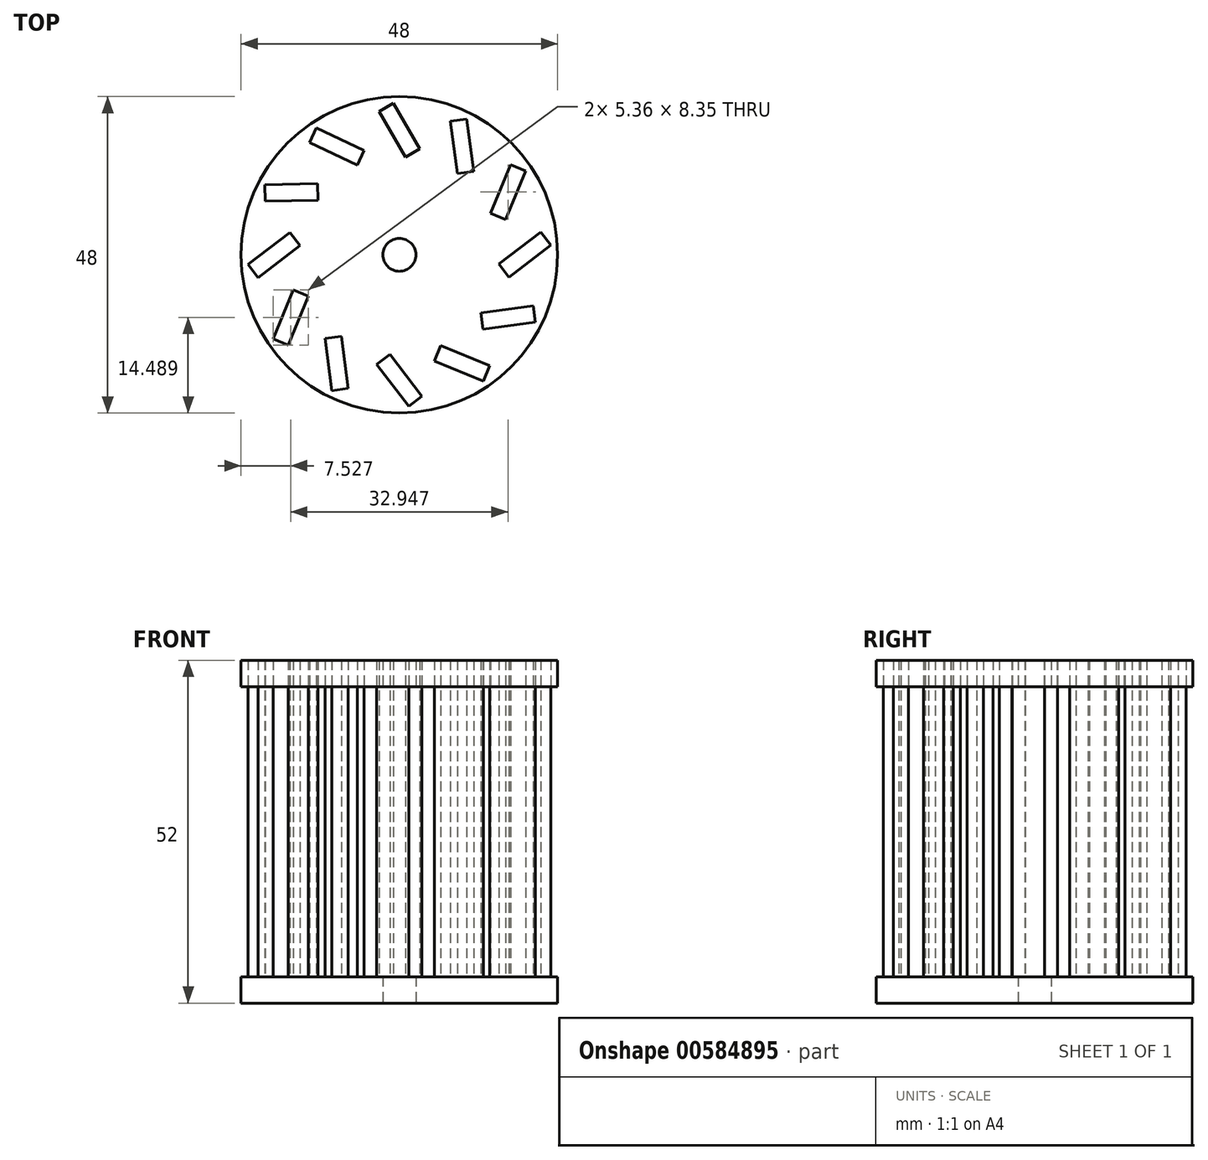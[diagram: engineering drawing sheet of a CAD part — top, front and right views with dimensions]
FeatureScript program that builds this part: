
annotation { "Feature Type Name" : "Feature", "Feature Type Description" : "" }
export const myFeature = defineFeature(function(context is Context, id is Id, definition is map)
    precondition{}
    {
        {
            var Q0;
            Q0=qCreatedBy(makeId("Top.planeOp"),FACE);
            var sketch = newSketch(context, id + "F0", { "sketchPlane" : qUnion([Q0])});
            skCircle(sketch, "E0", {"center": v(0, 0) * mm, "radius": 24 * mm});
            skArc(sketch, "E1", {"start": v(22.95, 1.48) * mm, "mid": v(-22.55, 4.53) * mm, "end": v(20.6, -10.23) * mm});
            skLineSegment(sketch, "E2", {"start": v(-3.08, 21.73) * mm, "end": v(-3.08, 14.8) * mm});
            skLineSegment(sketch, "E3", {"start": v(-3.08, 14.8) * mm, "end": v(0.92, 14.8) * mm});
            skLineSegment(sketch, "E4", {"start": v(0.92, 14.8) * mm, "end": v(-3.08, 21.73) * mm});
            skLineSegment(sketch, "E5", {"start": v(0.92, 14.8) * mm, "end": v(3.08, 16.05) * mm});
            skLineSegment(sketch, "E6", {"start": v(3.08, 16.05) * mm, "end": v(-0.92, 22.98) * mm});
            skLineSegment(sketch, "E7", {"start": v(-0.92, 22.98) * mm, "end": v(-3.08, 21.73) * mm});
            skLineSegment(sketch, "E8", {"start": v(-2, 22.36) * mm, "end": v(2, 15.43) * mm});
            skLineSegment(sketch, "E9", {"start": v(1.08, 19.52) * mm, "end": v(-1.08, 18.27) * mm});
            skPoint(sketch, "E10", {"position": v(0, 18.9) * mm});
            skLineSegment(sketch, "E11", {"start": v(1.04, 0.6) * mm, "end": v(-1.02, -0.59) * mm});
            skLineSegment(sketch, "E12.MirrorCS", {"start": v(-16.61, 3.4) * mm, "end": v(-22.95, -1.47) * mm});
            skLineSegment(sketch, "E13.MirrorCS", {"start": v(-15.09, 1.43) * mm, "end": v(-21.43, -3.46) * mm});
            skLineSegment(sketch, "E14.MirrorCS", {"start": v(-15.09, 1.43) * mm, "end": v(-16.61, 3.4) * mm});
            skLineSegment(sketch, "E15.MirrorCS", {"start": v(-22.95, -1.47) * mm, "end": v(-21.43, -3.46) * mm});
            skLineSegment(sketch, "E16.MirrorCS", {"start": v(-15.85, 2.42) * mm, "end": v(-22.2, -2.46) * mm});
            skLineSegment(sketch, "E17.MirrorCS", {"start": v(-18.23, -1) * mm, "end": v(-19.75, 1) * mm});
            skPoint(sketch, "E18.MirrorP", {"position": v(-18.99, 0) * mm});
            skLineSegment(sketch, "E19.MirrorCS", {"start": v(16.61, -3.4) * mm, "end": v(22.95, 1.48) * mm});
            skLineSegment(sketch, "E20.MirrorCS", {"start": v(15.1, -1.41) * mm, "end": v(21.43, 3.47) * mm});
            skLineSegment(sketch, "E21.MirrorCS", {"start": v(15.1, -1.41) * mm, "end": v(16.61, -3.4) * mm});
            skLineSegment(sketch, "E22.MirrorCS", {"start": v(22.95, 1.48) * mm, "end": v(21.43, 3.47) * mm});
            skLineSegment(sketch, "E23.MirrorCS", {"start": v(15.85, -2.4) * mm, "end": v(22.2, 2.48) * mm});
            skLineSegment(sketch, "E24.MirrorCS", {"start": v(18.22, 1) * mm, "end": v(19.74, -1) * mm});
            skPoint(sketch, "E25", {"position": v(18.98, 0) * mm});
            skLineSegment(sketch, "E26.MirrorCS", {"start": v(16.1, 5.34) * mm, "end": v(19.15, 12.73) * mm});
            skLineSegment(sketch, "E27.MirrorCS", {"start": v(13.8, 6.29) * mm, "end": v(16.84, 13.69) * mm});
            skLineSegment(sketch, "E28.MirrorCS", {"start": v(13.8, 6.29) * mm, "end": v(16.1, 5.34) * mm});
            skLineSegment(sketch, "E29.MirrorCS", {"start": v(19.15, 12.73) * mm, "end": v(16.84, 13.69) * mm});
            skLineSegment(sketch, "E30.MirrorCS", {"start": v(14.95, 5.81) * mm, "end": v(18, 13.2) * mm});
            skLineSegment(sketch, "E31.MirrorCS", {"start": v(15.32, 9.99) * mm, "end": v(17.63, 9.03) * mm});
            skPoint(sketch, "E32", {"position": v(16.47, 9.51) * mm});
            skLineSegment(sketch, "E33.MirrorCS", {"start": v(11.28, 12.67) * mm, "end": v(10.22, 20.6) * mm});
            skLineSegment(sketch, "E34.MirrorCS", {"start": v(8.8, 12.34) * mm, "end": v(7.74, 20.27) * mm});
            skLineSegment(sketch, "E35.MirrorCS", {"start": v(8.8, 12.34) * mm, "end": v(11.28, 12.67) * mm});
            skLineSegment(sketch, "E36.MirrorCS", {"start": v(10.22, 20.6) * mm, "end": v(7.74, 20.27) * mm});
            skLineSegment(sketch, "E37.MirrorCS", {"start": v(10.04, 12.5) * mm, "end": v(8.98, 20.44) * mm});
            skLineSegment(sketch, "E38.MirrorCS", {"start": v(8.27, 16.3) * mm, "end": v(10.75, 16.64) * mm});
            skPoint(sketch, "E39", {"position": v(9.51, 16.47) * mm});
            skLineSegment(sketch, "E40", {"start": v(-0.67, -1.16) * mm, "end": v(0.63, 1.1) * mm});
            skLineSegment(sketch, "E41", {"start": v(1.07, -0.62) * mm, "end": v(-1.13, 0.65) * mm});
            skLineSegment(sketch, "E42", {"start": v(0.67, -1.16) * mm, "end": v(-0.59, 1.02) * mm});
            skLineSegment(sketch, "E43.MirrorCS", {"start": v(12.67, -11.27) * mm, "end": v(20.6, -10.23) * mm});
            skLineSegment(sketch, "E44.MirrorCS", {"start": v(12.34, -8.8) * mm, "end": v(20.27, -7.75) * mm});
            skLineSegment(sketch, "E45.MirrorCS", {"start": v(12.34, -8.8) * mm, "end": v(12.67, -11.27) * mm});
            skLineSegment(sketch, "E46.MirrorCS", {"start": v(20.6, -10.23) * mm, "end": v(20.27, -7.75) * mm});
            skLineSegment(sketch, "E47.MirrorCS", {"start": v(12.5, -10.03) * mm, "end": v(20.44, -8.99) * mm});
            skLineSegment(sketch, "E48.MirrorCS", {"start": v(16.3, -8.27) * mm, "end": v(16.64, -10.75) * mm});
            skPoint(sketch, "E49", {"position": v(16.47, -9.51) * mm});
            skLineSegment(sketch, "E50.MirrorCS", {"start": v(5.34, -16.1) * mm, "end": v(12.73, -19.15) * mm});
            skLineSegment(sketch, "E51.MirrorCS", {"start": v(6.3, -13.8) * mm, "end": v(13.69, -16.84) * mm});
            skLineSegment(sketch, "E52.MirrorCS", {"start": v(6.3, -13.8) * mm, "end": v(5.34, -16.1) * mm});
            skLineSegment(sketch, "E53.MirrorCS", {"start": v(12.73, -19.15) * mm, "end": v(13.69, -16.84) * mm});
            skLineSegment(sketch, "E54.MirrorCS", {"start": v(5.81, -14.95) * mm, "end": v(13.2, -18) * mm});
            skLineSegment(sketch, "E55.MirrorCS", {"start": v(9.99, -15.32) * mm, "end": v(9.03, -17.63) * mm});
            skPoint(sketch, "E56", {"position": v(9.51, -16.47) * mm});
            skLineSegment(sketch, "E57.MirrorCS", {"start": v(-16.84, -13.69) * mm, "end": v(-13.8, -6.3) * mm});
            skLineSegment(sketch, "E58.MirrorCS", {"start": v(-19.15, -12.73) * mm, "end": v(-16.1, -5.34) * mm});
            skLineSegment(sketch, "E59.MirrorCS", {"start": v(-19.15, -12.73) * mm, "end": v(-16.84, -13.69) * mm});
            skLineSegment(sketch, "E60.MirrorCS", {"start": v(-13.8, -6.3) * mm, "end": v(-16.1, -5.34) * mm});
            skLineSegment(sketch, "E61.MirrorCS", {"start": v(-18, -13.2) * mm, "end": v(-14.95, -5.81) * mm});
            skLineSegment(sketch, "E62.MirrorCS", {"start": v(-17.63, -9.03) * mm, "end": v(-15.32, -9.99) * mm});
            skPoint(sketch, "E63", {"position": v(-16.47, -9.51) * mm});
            skLineSegment(sketch, "E64.MirrorCS", {"start": v(-7.74, -20.27) * mm, "end": v(-8.8, -12.34) * mm});
            skLineSegment(sketch, "E65.MirrorCS", {"start": v(-10.22, -20.6) * mm, "end": v(-11.28, -12.67) * mm});
            skLineSegment(sketch, "E66.MirrorCS", {"start": v(-10.22, -20.6) * mm, "end": v(-7.74, -20.27) * mm});
            skLineSegment(sketch, "E67.MirrorCS", {"start": v(-8.8, -12.34) * mm, "end": v(-11.28, -12.67) * mm});
            skLineSegment(sketch, "E68.MirrorCS", {"start": v(-8.98, -20.44) * mm, "end": v(-10.04, -12.5) * mm});
            skLineSegment(sketch, "E69.MirrorCS", {"start": v(-10.75, -16.64) * mm, "end": v(-8.27, -16.3) * mm});
            skPoint(sketch, "E70", {"position": v(-9.51, -16.47) * mm});
            skLineSegment(sketch, "E71.MirrorCS", {"start": v(-20.35, 8.11) * mm, "end": v(-12.35, 8.3) * mm});
            skLineSegment(sketch, "E72.MirrorCS", {"start": v(-20.4, 10.61) * mm, "end": v(-12.4, 10.8) * mm});
            skLineSegment(sketch, "E73.MirrorCS", {"start": v(-20.4, 10.61) * mm, "end": v(-20.35, 8.11) * mm});
            skLineSegment(sketch, "E74.MirrorCS", {"start": v(-12.35, 8.3) * mm, "end": v(-12.4, 10.8) * mm});
            skLineSegment(sketch, "E75.MirrorCS", {"start": v(-20.38, 9.36) * mm, "end": v(-12.38, 9.55) * mm});
            skLineSegment(sketch, "E76.MirrorCS", {"start": v(-16.4, 10.7) * mm, "end": v(-16.35, 8.2) * mm});
            skPoint(sketch, "E77", {"position": v(-16.38, 9.46) * mm});
            skLineSegment(sketch, "E78.MirrorCS", {"start": v(-13.63, 17) * mm, "end": v(-6.4, 13.59) * mm});
            skLineSegment(sketch, "E79.MirrorCS", {"start": v(-12.57, 19.26) * mm, "end": v(-5.33, 15.85) * mm});
            skLineSegment(sketch, "E80.MirrorCS", {"start": v(-12.57, 19.26) * mm, "end": v(-13.63, 17) * mm});
            skLineSegment(sketch, "E81.MirrorCS", {"start": v(-6.4, 13.59) * mm, "end": v(-5.33, 15.85) * mm});
            skLineSegment(sketch, "E82.MirrorCS", {"start": v(-13.1, 18.13) * mm, "end": v(-5.87, 14.72) * mm});
            skLineSegment(sketch, "E83.MirrorCS", {"start": v(-8.95, 17.56) * mm, "end": v(-10.02, 15.3) * mm});
            skPoint(sketch, "E84", {"position": v(-9.48, 16.43) * mm});
            skCircle(sketch, "E85", {"center": v(0, 0) * mm, "radius": 2.5 * mm});
            skLineSegment(sketch, "E86.MirrorCS", {"start": v(3.43, -21.43) * mm, "end": v(-1.45, -15.1) * mm});
            skLineSegment(sketch, "E87.MirrorCS", {"start": v(1.45, -22.95) * mm, "end": v(-3.43, -16.62) * mm});
            skLineSegment(sketch, "E88.MirrorCS", {"start": v(1.45, -22.95) * mm, "end": v(3.43, -21.43) * mm});
            skLineSegment(sketch, "E89.MirrorCS", {"start": v(-1.45, -15.1) * mm, "end": v(-3.43, -16.62) * mm});
            skLineSegment(sketch, "E90.MirrorCS", {"start": v(2.44, -22.2) * mm, "end": v(-2.44, -15.85) * mm});
            skLineSegment(sketch, "E91.MirrorCS", {"start": v(-1, -19.79) * mm, "end": v(1, -18.26) * mm});
            skPoint(sketch, "E92", {"position": v(0, -19.02) * mm});
            skSolve(sketch);
        }
        {
            var Q0;
            Q0=makeQuery(id+"F0.imprint","IMPRINT",FACE,{"disambiguationData":[TD([[makeQuery(id+"F0.imprint","IMPRINT",EDGE,{"derivedFrom":sQuery(id+"F0.wireOp",EDGE,"E0")}),1.0]])]});
            var Q1;
            {var subQ0=sQuery(id+"F0.wireOp",EDGE,"E2");Q1=makeQuery(id+"F0.imprint","IMPRINT",FACE,{"disambiguationData":[TD([[makeQuery(id+"F0.imprint","IMPRINT",EDGE,{"derivedFrom":subQ0}),1.0]])]});}
            extrude(context, id + "F1", {"entities" : qUnion([Q0, Q1]), "depth" : 4 * mm, "offsetDistance" : 25 * mm});
        }
        {
            var Q0;
            {var subQ0=sQuery(id+"F0.wireOp",EDGE,"E35.MirrorCS");var subQ1=sQuery(id+"F0.wireOp",EDGE,"E33.MirrorCS");var subQ2=makeQuery(id+"F0.imprint","INTERSECT",VERTEX,{"derivedFrom":[subQ1,subQ0]});Q0=makeQuery(id+"F0.imprint","IMPRINT",FACE,{"disambiguationData":[TD([[makeQuery(id+"F0.imprint","IMPRINT",EDGE,{"disambiguationData":[TD([[subQ2,-1.0]])],"derivedFrom":subQ1}),1.0]])]});}
            var Q1;
            {var subQ0=sQuery(id+"F0.wireOp",EDGE,"E35.MirrorCS");var subQ1=sQuery(id+"F0.wireOp",EDGE,"E34.MirrorCS");var subQ2=makeQuery(id+"F0.imprint","INTERSECT",VERTEX,{"derivedFrom":[subQ1,subQ0]});Q1=makeQuery(id+"F0.imprint","IMPRINT",FACE,{"disambiguationData":[TD([[makeQuery(id+"F0.imprint","IMPRINT",EDGE,{"disambiguationData":[TD([[subQ2,-1.0]])],"derivedFrom":subQ1}),-1.0]])]});}
            var Q2;
            {var subQ0=sQuery(id+"F0.wireOp",EDGE,"E36.MirrorCS");var subQ1=sQuery(id+"F0.wireOp",EDGE,"E33.MirrorCS");var subQ2=makeQuery(id+"F0.imprint","INTERSECT",VERTEX,{"derivedFrom":[subQ1,subQ0]});Q2=makeQuery(id+"F0.imprint","IMPRINT",FACE,{"disambiguationData":[TD([[makeQuery(id+"F0.imprint","IMPRINT",EDGE,{"disambiguationData":[TD([[subQ2,1.0]])],"derivedFrom":subQ1}),1.0]])]});}
            var Q3;
            {var subQ0=sQuery(id+"F0.wireOp",EDGE,"E36.MirrorCS");var subQ1=sQuery(id+"F0.wireOp",EDGE,"E34.MirrorCS");var subQ2=makeQuery(id+"F0.imprint","INTERSECT",VERTEX,{"derivedFrom":[subQ1,subQ0]});Q3=makeQuery(id+"F0.imprint","IMPRINT",FACE,{"disambiguationData":[TD([[makeQuery(id+"F0.imprint","IMPRINT",EDGE,{"disambiguationData":[TD([[subQ2,1.0]])],"derivedFrom":subQ1}),-1.0]])]});}
            var Q4;
            {var subQ0=sQuery(id+"F0.wireOp",EDGE,"E6");var subQ1=sQuery(id+"F0.wireOp",EDGE,"E5");var subQ2=makeQuery(id+"F0.imprint","INTERSECT",VERTEX,{"derivedFrom":[subQ1,subQ0]});Q4=makeQuery(id+"F0.imprint","IMPRINT",FACE,{"disambiguationData":[TD([[makeQuery(id+"F0.imprint","IMPRINT",EDGE,{"disambiguationData":[TD([[subQ2,1.0]])],"derivedFrom":subQ1}),1.0]])]});}
            var Q5;
            {var subQ0=sQuery(id+"F0.wireOp",EDGE,"E5");var subQ5=sQuery(id+"F0.wireOp",EDGE,"E8");var subQ6=makeQuery(id+"F0.imprint","INTERSECT",VERTEX,{"derivedFrom":[subQ0,subQ5]});Q5=makeQuery(id+"F0.imprint","IMPRINT",FACE,{"disambiguationData":[TD([[makeQuery(id+"F0.imprint","IMPRINT",EDGE,{"disambiguationData":[TD([[subQ6,1.0]])],"derivedFrom":subQ5}),-1.0]])]});}
            var Q6;
            {var subQ0=sQuery(id+"F0.wireOp",EDGE,"E7");var subQ1=sQuery(id+"F0.wireOp",EDGE,"E6");var subQ2=makeQuery(id+"F0.imprint","INTERSECT",VERTEX,{"derivedFrom":[subQ1,subQ0]});Q6=makeQuery(id+"F0.imprint","IMPRINT",FACE,{"disambiguationData":[TD([[makeQuery(id+"F0.imprint","IMPRINT",EDGE,{"disambiguationData":[TD([[subQ2,1.0]])],"derivedFrom":subQ1}),1.0]])]});}
            var Q7;
            {var subQ0=sQuery(id+"F0.wireOp",EDGE,"E7");var subQ5=sQuery(id+"F0.wireOp",EDGE,"E8");var subQ7=makeQuery(id+"F0.imprint","INTERSECT",VERTEX,{"derivedFrom":[subQ0,subQ5]});Q7=makeQuery(id+"F0.imprint","IMPRINT",FACE,{"disambiguationData":[TD([[makeQuery(id+"F0.imprint","IMPRINT",EDGE,{"disambiguationData":[TD([[subQ7,-1.0]])],"derivedFrom":subQ5}),-1.0]])]});}
            var Q8;
            {var subQ0=sQuery(id+"F0.wireOp",EDGE,"E80.MirrorCS");var subQ1=sQuery(id+"F0.wireOp",EDGE,"E79.MirrorCS");var subQ2=makeQuery(id+"F0.imprint","INTERSECT",VERTEX,{"derivedFrom":[subQ1,subQ0]});Q8=makeQuery(id+"F0.imprint","IMPRINT",FACE,{"disambiguationData":[TD([[makeQuery(id+"F0.imprint","IMPRINT",EDGE,{"disambiguationData":[TD([[subQ2,-1.0]])],"derivedFrom":subQ1}),-1.0]])]});}
            var Q9;
            {var subQ0=sQuery(id+"F0.wireOp",EDGE,"E80.MirrorCS");var subQ1=sQuery(id+"F0.wireOp",EDGE,"E78.MirrorCS");var subQ2=makeQuery(id+"F0.imprint","INTERSECT",VERTEX,{"derivedFrom":[subQ1,subQ0]});Q9=makeQuery(id+"F0.imprint","IMPRINT",FACE,{"disambiguationData":[TD([[makeQuery(id+"F0.imprint","IMPRINT",EDGE,{"disambiguationData":[TD([[subQ2,-1.0]])],"derivedFrom":subQ1}),1.0]])]});}
            var Q10;
            {var subQ0=sQuery(id+"F0.wireOp",EDGE,"E81.MirrorCS");var subQ1=sQuery(id+"F0.wireOp",EDGE,"E79.MirrorCS");var subQ2=makeQuery(id+"F0.imprint","INTERSECT",VERTEX,{"derivedFrom":[subQ1,subQ0]});Q10=makeQuery(id+"F0.imprint","IMPRINT",FACE,{"disambiguationData":[TD([[makeQuery(id+"F0.imprint","IMPRINT",EDGE,{"disambiguationData":[TD([[subQ2,1.0]])],"derivedFrom":subQ1}),-1.0]])]});}
            var Q11;
            {var subQ0=sQuery(id+"F0.wireOp",EDGE,"E81.MirrorCS");var subQ1=sQuery(id+"F0.wireOp",EDGE,"E78.MirrorCS");var subQ2=makeQuery(id+"F0.imprint","INTERSECT",VERTEX,{"derivedFrom":[subQ1,subQ0]});Q11=makeQuery(id+"F0.imprint","IMPRINT",FACE,{"disambiguationData":[TD([[makeQuery(id+"F0.imprint","IMPRINT",EDGE,{"disambiguationData":[TD([[subQ2,1.0]])],"derivedFrom":subQ1}),1.0]])]});}
            var Q12;
            {var subQ0=sQuery(id+"F0.wireOp",EDGE,"E74.MirrorCS");var subQ1=sQuery(id+"F0.wireOp",EDGE,"E72.MirrorCS");var subQ2=makeQuery(id+"F0.imprint","INTERSECT",VERTEX,{"derivedFrom":[subQ1,subQ0]});Q12=makeQuery(id+"F0.imprint","IMPRINT",FACE,{"disambiguationData":[TD([[makeQuery(id+"F0.imprint","IMPRINT",EDGE,{"disambiguationData":[TD([[subQ2,1.0]])],"derivedFrom":subQ1}),-1.0]])]});}
            var Q13;
            {var subQ0=sQuery(id+"F0.wireOp",EDGE,"E73.MirrorCS");var subQ1=sQuery(id+"F0.wireOp",EDGE,"E72.MirrorCS");var subQ2=makeQuery(id+"F0.imprint","INTERSECT",VERTEX,{"derivedFrom":[subQ1,subQ0]});Q13=makeQuery(id+"F0.imprint","IMPRINT",FACE,{"disambiguationData":[TD([[makeQuery(id+"F0.imprint","IMPRINT",EDGE,{"disambiguationData":[TD([[subQ2,-1.0]])],"derivedFrom":subQ1}),-1.0]])]});}
            var Q14;
            {var subQ0=sQuery(id+"F0.wireOp",EDGE,"E73.MirrorCS");var subQ1=sQuery(id+"F0.wireOp",EDGE,"E71.MirrorCS");var subQ2=makeQuery(id+"F0.imprint","INTERSECT",VERTEX,{"derivedFrom":[subQ1,subQ0]});Q14=makeQuery(id+"F0.imprint","IMPRINT",FACE,{"disambiguationData":[TD([[makeQuery(id+"F0.imprint","IMPRINT",EDGE,{"disambiguationData":[TD([[subQ2,-1.0]])],"derivedFrom":subQ1}),1.0]])]});}
            var Q15;
            {var subQ0=sQuery(id+"F0.wireOp",EDGE,"E74.MirrorCS");var subQ1=sQuery(id+"F0.wireOp",EDGE,"E71.MirrorCS");var subQ2=makeQuery(id+"F0.imprint","INTERSECT",VERTEX,{"derivedFrom":[subQ1,subQ0]});Q15=makeQuery(id+"F0.imprint","IMPRINT",FACE,{"disambiguationData":[TD([[makeQuery(id+"F0.imprint","IMPRINT",EDGE,{"disambiguationData":[TD([[subQ2,1.0]])],"derivedFrom":subQ1}),1.0]])]});}
            var Q16;
            {var subQ0=sQuery(id+"F0.wireOp",EDGE,"E14.MirrorCS");var subQ1=sQuery(id+"F0.wireOp",EDGE,"E12.MirrorCS");var subQ2=makeQuery(id+"F0.imprint","INTERSECT",VERTEX,{"derivedFrom":[subQ1,subQ0]});Q16=makeQuery(id+"F0.imprint","IMPRINT",FACE,{"disambiguationData":[TD([[makeQuery(id+"F0.imprint","IMPRINT",EDGE,{"disambiguationData":[TD([[subQ2,-1.0]])],"derivedFrom":subQ1}),1.0]])]});}
            var Q17;
            {var subQ0=sQuery(id+"F0.wireOp",EDGE,"E15.MirrorCS");var subQ1=sQuery(id+"F0.wireOp",EDGE,"E12.MirrorCS");var subQ2=makeQuery(id+"F0.imprint","INTERSECT",VERTEX,{"derivedFrom":[subQ1,subQ0]});Q17=makeQuery(id+"F0.imprint","IMPRINT",FACE,{"disambiguationData":[TD([[makeQuery(id+"F0.imprint","IMPRINT",EDGE,{"disambiguationData":[TD([[subQ2,1.0]])],"derivedFrom":subQ1}),1.0]])]});}
            var Q18;
            {var subQ0=sQuery(id+"F0.wireOp",EDGE,"E15.MirrorCS");var subQ1=sQuery(id+"F0.wireOp",EDGE,"E13.MirrorCS");var subQ2=makeQuery(id+"F0.imprint","INTERSECT",VERTEX,{"derivedFrom":[subQ1,subQ0]});Q18=makeQuery(id+"F0.imprint","IMPRINT",FACE,{"disambiguationData":[TD([[makeQuery(id+"F0.imprint","IMPRINT",EDGE,{"disambiguationData":[TD([[subQ2,1.0]])],"derivedFrom":subQ1}),-1.0]])]});}
            var Q19;
            {var subQ0=sQuery(id+"F0.wireOp",EDGE,"E14.MirrorCS");var subQ1=sQuery(id+"F0.wireOp",EDGE,"E13.MirrorCS");var subQ2=makeQuery(id+"F0.imprint","INTERSECT",VERTEX,{"derivedFrom":[subQ1,subQ0]});Q19=makeQuery(id+"F0.imprint","IMPRINT",FACE,{"disambiguationData":[TD([[makeQuery(id+"F0.imprint","IMPRINT",EDGE,{"disambiguationData":[TD([[subQ2,-1.0]])],"derivedFrom":subQ1}),-1.0]])]});}
            var Q20;
            {var subQ0=sQuery(id+"F0.wireOp",EDGE,"E60.MirrorCS");var subQ1=sQuery(id+"F0.wireOp",EDGE,"E58.MirrorCS");var subQ2=makeQuery(id+"F0.imprint","INTERSECT",VERTEX,{"derivedFrom":[subQ1,subQ0]});Q20=makeQuery(id+"F0.imprint","IMPRINT",FACE,{"disambiguationData":[TD([[makeQuery(id+"F0.imprint","IMPRINT",EDGE,{"disambiguationData":[TD([[subQ2,1.0]])],"derivedFrom":subQ1}),-1.0]])]});}
            var Q21;
            {var subQ0=sQuery(id+"F0.wireOp",EDGE,"E60.MirrorCS");var subQ1=sQuery(id+"F0.wireOp",EDGE,"E57.MirrorCS");var subQ2=makeQuery(id+"F0.imprint","INTERSECT",VERTEX,{"derivedFrom":[subQ1,subQ0]});Q21=makeQuery(id+"F0.imprint","IMPRINT",FACE,{"disambiguationData":[TD([[makeQuery(id+"F0.imprint","IMPRINT",EDGE,{"disambiguationData":[TD([[subQ2,1.0]])],"derivedFrom":subQ1}),1.0]])]});}
            var Q22;
            {var subQ0=sQuery(id+"F0.wireOp",EDGE,"E59.MirrorCS");var subQ1=sQuery(id+"F0.wireOp",EDGE,"E57.MirrorCS");var subQ2=makeQuery(id+"F0.imprint","INTERSECT",VERTEX,{"derivedFrom":[subQ1,subQ0]});Q22=makeQuery(id+"F0.imprint","IMPRINT",FACE,{"disambiguationData":[TD([[makeQuery(id+"F0.imprint","IMPRINT",EDGE,{"disambiguationData":[TD([[subQ2,-1.0]])],"derivedFrom":subQ1}),1.0]])]});}
            var Q23;
            {var subQ0=sQuery(id+"F0.wireOp",EDGE,"E59.MirrorCS");var subQ1=sQuery(id+"F0.wireOp",EDGE,"E58.MirrorCS");var subQ2=makeQuery(id+"F0.imprint","INTERSECT",VERTEX,{"derivedFrom":[subQ1,subQ0]});Q23=makeQuery(id+"F0.imprint","IMPRINT",FACE,{"disambiguationData":[TD([[makeQuery(id+"F0.imprint","IMPRINT",EDGE,{"disambiguationData":[TD([[subQ2,-1.0]])],"derivedFrom":subQ1}),-1.0]])]});}
            var Q24;
            {var subQ0=sQuery(id+"F0.wireOp",EDGE,"E66.MirrorCS");var subQ1=sQuery(id+"F0.wireOp",EDGE,"E65.MirrorCS");var subQ2=makeQuery(id+"F0.imprint","INTERSECT",VERTEX,{"derivedFrom":[subQ1,subQ0]});Q24=makeQuery(id+"F0.imprint","IMPRINT",FACE,{"disambiguationData":[TD([[makeQuery(id+"F0.imprint","IMPRINT",EDGE,{"disambiguationData":[TD([[subQ2,-1.0]])],"derivedFrom":subQ1}),-1.0]])]});}
            var Q25;
            {var subQ0=sQuery(id+"F0.wireOp",EDGE,"E66.MirrorCS");var subQ1=sQuery(id+"F0.wireOp",EDGE,"E64.MirrorCS");var subQ2=makeQuery(id+"F0.imprint","INTERSECT",VERTEX,{"derivedFrom":[subQ1,subQ0]});Q25=makeQuery(id+"F0.imprint","IMPRINT",FACE,{"disambiguationData":[TD([[makeQuery(id+"F0.imprint","IMPRINT",EDGE,{"disambiguationData":[TD([[subQ2,-1.0]])],"derivedFrom":subQ1}),1.0]])]});}
            var Q26;
            {var subQ0=sQuery(id+"F0.wireOp",EDGE,"E67.MirrorCS");var subQ1=sQuery(id+"F0.wireOp",EDGE,"E65.MirrorCS");var subQ2=makeQuery(id+"F0.imprint","INTERSECT",VERTEX,{"derivedFrom":[subQ1,subQ0]});Q26=makeQuery(id+"F0.imprint","IMPRINT",FACE,{"disambiguationData":[TD([[makeQuery(id+"F0.imprint","IMPRINT",EDGE,{"disambiguationData":[TD([[subQ2,1.0]])],"derivedFrom":subQ1}),-1.0]])]});}
            var Q27;
            {var subQ0=sQuery(id+"F0.wireOp",EDGE,"E67.MirrorCS");var subQ1=sQuery(id+"F0.wireOp",EDGE,"E64.MirrorCS");var subQ2=makeQuery(id+"F0.imprint","INTERSECT",VERTEX,{"derivedFrom":[subQ1,subQ0]});Q27=makeQuery(id+"F0.imprint","IMPRINT",FACE,{"disambiguationData":[TD([[makeQuery(id+"F0.imprint","IMPRINT",EDGE,{"disambiguationData":[TD([[subQ2,1.0]])],"derivedFrom":subQ1}),1.0]])]});}
            var Q28;
            {var subQ0=sQuery(id+"F0.wireOp",EDGE,"E89.MirrorCS");var subQ1=sQuery(id+"F0.wireOp",EDGE,"E87.MirrorCS");var subQ2=makeQuery(id+"F0.imprint","INTERSECT",VERTEX,{"derivedFrom":[subQ1,subQ0]});Q28=makeQuery(id+"F0.imprint","IMPRINT",FACE,{"disambiguationData":[TD([[makeQuery(id+"F0.imprint","IMPRINT",EDGE,{"disambiguationData":[TD([[subQ2,1.0]])],"derivedFrom":subQ1}),-1.0]])]});}
            var Q29;
            {var subQ0=sQuery(id+"F0.wireOp",EDGE,"E89.MirrorCS");var subQ1=sQuery(id+"F0.wireOp",EDGE,"E86.MirrorCS");var subQ2=makeQuery(id+"F0.imprint","INTERSECT",VERTEX,{"derivedFrom":[subQ1,subQ0]});Q29=makeQuery(id+"F0.imprint","IMPRINT",FACE,{"disambiguationData":[TD([[makeQuery(id+"F0.imprint","IMPRINT",EDGE,{"disambiguationData":[TD([[subQ2,1.0]])],"derivedFrom":subQ1}),1.0]])]});}
            var Q30;
            {var subQ0=sQuery(id+"F0.wireOp",EDGE,"E88.MirrorCS");var subQ1=sQuery(id+"F0.wireOp",EDGE,"E86.MirrorCS");var subQ2=makeQuery(id+"F0.imprint","INTERSECT",VERTEX,{"derivedFrom":[subQ1,subQ0]});Q30=makeQuery(id+"F0.imprint","IMPRINT",FACE,{"disambiguationData":[TD([[makeQuery(id+"F0.imprint","IMPRINT",EDGE,{"disambiguationData":[TD([[subQ2,-1.0]])],"derivedFrom":subQ1}),1.0]])]});}
            var Q31;
            {var subQ0=sQuery(id+"F0.wireOp",EDGE,"E88.MirrorCS");var subQ1=sQuery(id+"F0.wireOp",EDGE,"E87.MirrorCS");var subQ2=makeQuery(id+"F0.imprint","INTERSECT",VERTEX,{"derivedFrom":[subQ1,subQ0]});Q31=makeQuery(id+"F0.imprint","IMPRINT",FACE,{"disambiguationData":[TD([[makeQuery(id+"F0.imprint","IMPRINT",EDGE,{"disambiguationData":[TD([[subQ2,-1.0]])],"derivedFrom":subQ1}),-1.0]])]});}
            var Q32;
            {var subQ0=sQuery(id+"F0.wireOp",EDGE,"E53.MirrorCS");var subQ1=sQuery(id+"F0.wireOp",EDGE,"E50.MirrorCS");var subQ2=makeQuery(id+"F0.imprint","INTERSECT",VERTEX,{"derivedFrom":[subQ1,subQ0]});Q32=makeQuery(id+"F0.imprint","IMPRINT",FACE,{"disambiguationData":[TD([[makeQuery(id+"F0.imprint","IMPRINT",EDGE,{"disambiguationData":[TD([[subQ2,1.0]])],"derivedFrom":subQ1}),1.0]])]});}
            var Q33;
            {var subQ0=sQuery(id+"F0.wireOp",EDGE,"E52.MirrorCS");var subQ1=sQuery(id+"F0.wireOp",EDGE,"E50.MirrorCS");var subQ2=makeQuery(id+"F0.imprint","INTERSECT",VERTEX,{"derivedFrom":[subQ1,subQ0]});Q33=makeQuery(id+"F0.imprint","IMPRINT",FACE,{"disambiguationData":[TD([[makeQuery(id+"F0.imprint","IMPRINT",EDGE,{"disambiguationData":[TD([[subQ2,-1.0]])],"derivedFrom":subQ1}),1.0]])]});}
            var Q34;
            {var subQ0=sQuery(id+"F0.wireOp",EDGE,"E52.MirrorCS");var subQ1=sQuery(id+"F0.wireOp",EDGE,"E51.MirrorCS");var subQ2=makeQuery(id+"F0.imprint","INTERSECT",VERTEX,{"derivedFrom":[subQ1,subQ0]});Q34=makeQuery(id+"F0.imprint","IMPRINT",FACE,{"disambiguationData":[TD([[makeQuery(id+"F0.imprint","IMPRINT",EDGE,{"disambiguationData":[TD([[subQ2,-1.0]])],"derivedFrom":subQ1}),-1.0]])]});}
            var Q35;
            {var subQ0=sQuery(id+"F0.wireOp",EDGE,"E53.MirrorCS");var subQ1=sQuery(id+"F0.wireOp",EDGE,"E51.MirrorCS");var subQ2=makeQuery(id+"F0.imprint","INTERSECT",VERTEX,{"derivedFrom":[subQ1,subQ0]});Q35=makeQuery(id+"F0.imprint","IMPRINT",FACE,{"disambiguationData":[TD([[makeQuery(id+"F0.imprint","IMPRINT",EDGE,{"disambiguationData":[TD([[subQ2,1.0]])],"derivedFrom":subQ1}),-1.0]])]});}
            var Q36;
            {var subQ0=sQuery(id+"F0.wireOp",EDGE,"E45.MirrorCS");var subQ1=sQuery(id+"F0.wireOp",EDGE,"E43.MirrorCS");var subQ2=makeQuery(id+"F0.imprint","INTERSECT",VERTEX,{"derivedFrom":[subQ1,subQ0]});Q36=makeQuery(id+"F0.imprint","IMPRINT",FACE,{"disambiguationData":[TD([[makeQuery(id+"F0.imprint","IMPRINT",EDGE,{"disambiguationData":[TD([[subQ2,-1.0]])],"derivedFrom":subQ1}),1.0]])]});}
            var Q37;
            {var subQ0=sQuery(id+"F0.wireOp",EDGE,"E46.MirrorCS");var subQ1=sQuery(id+"F0.wireOp",EDGE,"E43.MirrorCS");var subQ2=makeQuery(id+"F0.imprint","INTERSECT",VERTEX,{"derivedFrom":[subQ1,subQ0]});Q37=makeQuery(id+"F0.imprint","IMPRINT",FACE,{"disambiguationData":[TD([[makeQuery(id+"F0.imprint","IMPRINT",EDGE,{"disambiguationData":[TD([[subQ2,1.0]])],"derivedFrom":subQ1}),1.0]])]});}
            var Q38;
            {var subQ0=sQuery(id+"F0.wireOp",EDGE,"E45.MirrorCS");var subQ1=sQuery(id+"F0.wireOp",EDGE,"E44.MirrorCS");var subQ2=makeQuery(id+"F0.imprint","INTERSECT",VERTEX,{"derivedFrom":[subQ1,subQ0]});Q38=makeQuery(id+"F0.imprint","IMPRINT",FACE,{"disambiguationData":[TD([[makeQuery(id+"F0.imprint","IMPRINT",EDGE,{"disambiguationData":[TD([[subQ2,-1.0]])],"derivedFrom":subQ1}),-1.0]])]});}
            var Q39;
            {var subQ0=sQuery(id+"F0.wireOp",EDGE,"E46.MirrorCS");var subQ1=sQuery(id+"F0.wireOp",EDGE,"E44.MirrorCS");var subQ2=makeQuery(id+"F0.imprint","INTERSECT",VERTEX,{"derivedFrom":[subQ1,subQ0]});Q39=makeQuery(id+"F0.imprint","IMPRINT",FACE,{"disambiguationData":[TD([[makeQuery(id+"F0.imprint","IMPRINT",EDGE,{"disambiguationData":[TD([[subQ2,1.0]])],"derivedFrom":subQ1}),-1.0]])]});}
            var Q40;
            {var subQ0=sQuery(id+"F0.wireOp",EDGE,"E21.MirrorCS");var subQ1=sQuery(id+"F0.wireOp",EDGE,"E19.MirrorCS");var subQ2=makeQuery(id+"F0.imprint","INTERSECT",VERTEX,{"derivedFrom":[subQ1,subQ0]});Q40=makeQuery(id+"F0.imprint","IMPRINT",FACE,{"disambiguationData":[TD([[makeQuery(id+"F0.imprint","IMPRINT",EDGE,{"disambiguationData":[TD([[subQ2,-1.0]])],"derivedFrom":subQ1}),1.0]])]});}
            var Q41;
            {var subQ0=sQuery(id+"F0.wireOp",EDGE,"E22.MirrorCS");var subQ1=sQuery(id+"F0.wireOp",EDGE,"E19.MirrorCS");var subQ2=makeQuery(id+"F0.imprint","INTERSECT",VERTEX,{"derivedFrom":[subQ1,subQ0]});Q41=makeQuery(id+"F0.imprint","IMPRINT",FACE,{"disambiguationData":[TD([[makeQuery(id+"F0.imprint","IMPRINT",EDGE,{"disambiguationData":[TD([[subQ2,1.0]])],"derivedFrom":subQ1}),1.0]])]});}
            var Q42;
            {var subQ0=sQuery(id+"F0.wireOp",EDGE,"E22.MirrorCS");var subQ1=sQuery(id+"F0.wireOp",EDGE,"E20.MirrorCS");var subQ2=makeQuery(id+"F0.imprint","INTERSECT",VERTEX,{"derivedFrom":[subQ1,subQ0]});Q42=makeQuery(id+"F0.imprint","IMPRINT",FACE,{"disambiguationData":[TD([[makeQuery(id+"F0.imprint","IMPRINT",EDGE,{"disambiguationData":[TD([[subQ2,1.0]])],"derivedFrom":subQ1}),-1.0]])]});}
            var Q43;
            {var subQ0=sQuery(id+"F0.wireOp",EDGE,"E21.MirrorCS");var subQ1=sQuery(id+"F0.wireOp",EDGE,"E20.MirrorCS");var subQ2=makeQuery(id+"F0.imprint","INTERSECT",VERTEX,{"derivedFrom":[subQ1,subQ0]});Q43=makeQuery(id+"F0.imprint","IMPRINT",FACE,{"disambiguationData":[TD([[makeQuery(id+"F0.imprint","IMPRINT",EDGE,{"disambiguationData":[TD([[subQ2,-1.0]])],"derivedFrom":subQ1}),-1.0]])]});}
            var Q44;
            {var subQ0=sQuery(id+"F0.wireOp",EDGE,"E28.MirrorCS");var subQ1=sQuery(id+"F0.wireOp",EDGE,"E26.MirrorCS");var subQ2=makeQuery(id+"F0.imprint","INTERSECT",VERTEX,{"derivedFrom":[subQ1,subQ0]});Q44=makeQuery(id+"F0.imprint","IMPRINT",FACE,{"disambiguationData":[TD([[makeQuery(id+"F0.imprint","IMPRINT",EDGE,{"disambiguationData":[TD([[subQ2,-1.0]])],"derivedFrom":subQ1}),1.0]])]});}
            var Q45;
            {var subQ0=sQuery(id+"F0.wireOp",EDGE,"E28.MirrorCS");var subQ1=sQuery(id+"F0.wireOp",EDGE,"E27.MirrorCS");var subQ2=makeQuery(id+"F0.imprint","INTERSECT",VERTEX,{"derivedFrom":[subQ1,subQ0]});Q45=makeQuery(id+"F0.imprint","IMPRINT",FACE,{"disambiguationData":[TD([[makeQuery(id+"F0.imprint","IMPRINT",EDGE,{"disambiguationData":[TD([[subQ2,-1.0]])],"derivedFrom":subQ1}),-1.0]])]});}
            var Q46;
            {var subQ0=sQuery(id+"F0.wireOp",EDGE,"E29.MirrorCS");var subQ1=sQuery(id+"F0.wireOp",EDGE,"E27.MirrorCS");var subQ2=makeQuery(id+"F0.imprint","INTERSECT",VERTEX,{"derivedFrom":[subQ1,subQ0]});Q46=makeQuery(id+"F0.imprint","IMPRINT",FACE,{"disambiguationData":[TD([[makeQuery(id+"F0.imprint","IMPRINT",EDGE,{"disambiguationData":[TD([[subQ2,1.0]])],"derivedFrom":subQ1}),-1.0]])]});}
            var Q47;
            {var subQ0=sQuery(id+"F0.wireOp",EDGE,"E29.MirrorCS");var subQ1=sQuery(id+"F0.wireOp",EDGE,"E26.MirrorCS");var subQ2=makeQuery(id+"F0.imprint","INTERSECT",VERTEX,{"derivedFrom":[subQ1,subQ0]});Q47=makeQuery(id+"F0.imprint","IMPRINT",FACE,{"disambiguationData":[TD([[makeQuery(id+"F0.imprint","IMPRINT",EDGE,{"disambiguationData":[TD([[subQ2,1.0]])],"derivedFrom":subQ1}),1.0]])]});}
            extrude(context, id + "F2", {"entities" : qUnion([Q0, Q1, Q2, Q3, Q4, Q5, Q6, Q7, Q8, Q9, Q10, Q11, Q12, Q13, Q14, Q15, Q16, Q17, Q18, Q19, Q20, Q21, Q22, Q23, Q24, Q25, Q26, Q27, Q28, Q29, Q30, Q31, Q32, Q33, Q34, Q35, Q36, Q37, Q38, Q39, Q40, Q41, Q42, Q43, Q44, Q45, Q46, Q47]), "operationType" : NewBodyOperationType.ADD, "depth" : 52 * mm, "offsetDistance" : 25 * mm});
        }
        {
            var Q0;
            Q0=makeQuery(id+"F1.opExtrude","CAP_FACE",FACE,{"disambiguationData":[OSD([sQuery(id+"F0.wireOp",EDGE,"E0"),sQuery(id+"F0.wireOp",EDGE,"E4"),sQuery(id+"F0.wireOp",EDGE,"E5"),sQuery(id+"F0.wireOp",EDGE,"E6"),sQuery(id+"F0.wireOp",EDGE,"E7"),sQuery(id+"F0.wireOp",EDGE,"E12.MirrorCS"),sQuery(id+"F0.wireOp",EDGE,"E13.MirrorCS"),sQuery(id+"F0.wireOp",EDGE,"E14.MirrorCS"),sQuery(id+"F0.wireOp",EDGE,"E15.MirrorCS"),sQuery(id+"F0.wireOp",EDGE,"E19.MirrorCS"),sQuery(id+"F0.wireOp",EDGE,"E20.MirrorCS"),sQuery(id+"F0.wireOp",EDGE,"E21.MirrorCS"),sQuery(id+"F0.wireOp",EDGE,"E22.MirrorCS"),sQuery(id+"F0.wireOp",EDGE,"E26.MirrorCS"),sQuery(id+"F0.wireOp",EDGE,"E27.MirrorCS"),sQuery(id+"F0.wireOp",EDGE,"E28.MirrorCS"),sQuery(id+"F0.wireOp",EDGE,"E29.MirrorCS"),sQuery(id+"F0.wireOp",EDGE,"E33.MirrorCS"),sQuery(id+"F0.wireOp",EDGE,"E34.MirrorCS"),sQuery(id+"F0.wireOp",EDGE,"E35.MirrorCS"),sQuery(id+"F0.wireOp",EDGE,"E36.MirrorCS"),sQuery(id+"F0.wireOp",EDGE,"E43.MirrorCS"),sQuery(id+"F0.wireOp",EDGE,"E44.MirrorCS"),sQuery(id+"F0.wireOp",EDGE,"E45.MirrorCS"),sQuery(id+"F0.wireOp",EDGE,"E46.MirrorCS"),sQuery(id+"F0.wireOp",EDGE,"E50.MirrorCS"),sQuery(id+"F0.wireOp",EDGE,"E51.MirrorCS"),sQuery(id+"F0.wireOp",EDGE,"E52.MirrorCS"),sQuery(id+"F0.wireOp",EDGE,"E53.MirrorCS"),sQuery(id+"F0.wireOp",EDGE,"E57.MirrorCS"),sQuery(id+"F0.wireOp",EDGE,"E58.MirrorCS"),sQuery(id+"F0.wireOp",EDGE,"E59.MirrorCS"),sQuery(id+"F0.wireOp",EDGE,"E60.MirrorCS"),sQuery(id+"F0.wireOp",EDGE,"E64.MirrorCS"),sQuery(id+"F0.wireOp",EDGE,"E65.MirrorCS"),sQuery(id+"F0.wireOp",EDGE,"E66.MirrorCS"),sQuery(id+"F0.wireOp",EDGE,"E67.MirrorCS"),sQuery(id+"F0.wireOp",EDGE,"E71.MirrorCS"),sQuery(id+"F0.wireOp",EDGE,"E72.MirrorCS"),sQuery(id+"F0.wireOp",EDGE,"E73.MirrorCS"),sQuery(id+"F0.wireOp",EDGE,"E74.MirrorCS"),sQuery(id+"F0.wireOp",EDGE,"E78.MirrorCS"),sQuery(id+"F0.wireOp",EDGE,"E79.MirrorCS"),sQuery(id+"F0.wireOp",EDGE,"E80.MirrorCS"),sQuery(id+"F0.wireOp",EDGE,"E81.MirrorCS"),sQuery(id+"F0.wireOp",EDGE,"E85"),sQuery(id+"F0.wireOp",EDGE,"E86.MirrorCS"),sQuery(id+"F0.wireOp",EDGE,"E87.MirrorCS"),sQuery(id+"F0.wireOp",EDGE,"E88.MirrorCS"),sQuery(id+"F0.wireOp",EDGE,"E89.MirrorCS")])],"isStart":false});
            extrude(context, id + "F3", {"entities" : qUnion([Q0]), "depth" : 48 * mm, "offsetDistance" : 25 * mm, "hasSecondDirection" : true, "secondDirectionOppositeDirection" : true, "secondDirectionDepth" : -44 * mm});
        }
    });
